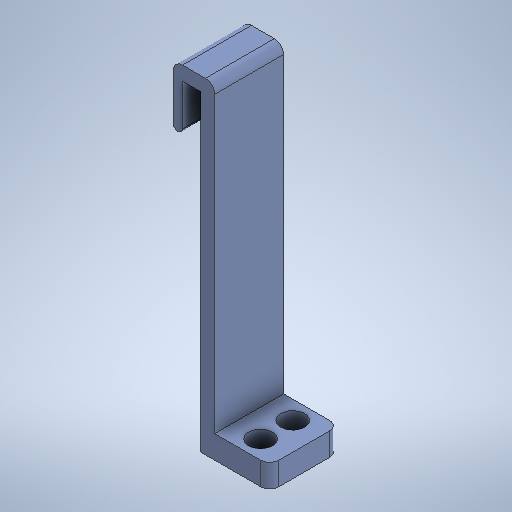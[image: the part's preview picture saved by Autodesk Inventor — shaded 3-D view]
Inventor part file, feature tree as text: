
AUTODESK INVENTOR PART (.ipt)
format: ipt  version: 2025 (Build 290162000, 162)  size: 623,104 bytes
history: native  units: mm
features: fillet x3, extrude x2, sketch x2
ambient origin geometry x8: Origin, YZ Plane, XZ Plane, XY Plane, X Axis, Y Axis, Z Axis, Center Point
bodies: Solide1 (feature_tree)
feature tree (7):
  extrude  "Extrusion1"  Depth=15.0mm TaperAngle=0.0deg
  extrude  "Extrusion2"  Depth=5.2mm
  fillet  "Congé2"  Radius=5.2mm
  fillet  "Congé3"  Radius=4.0mm
  fillet  "Congé4"  Radius=4.0mm
  sketch  "Esquisse1"
  sketch  "Esquisse2"
